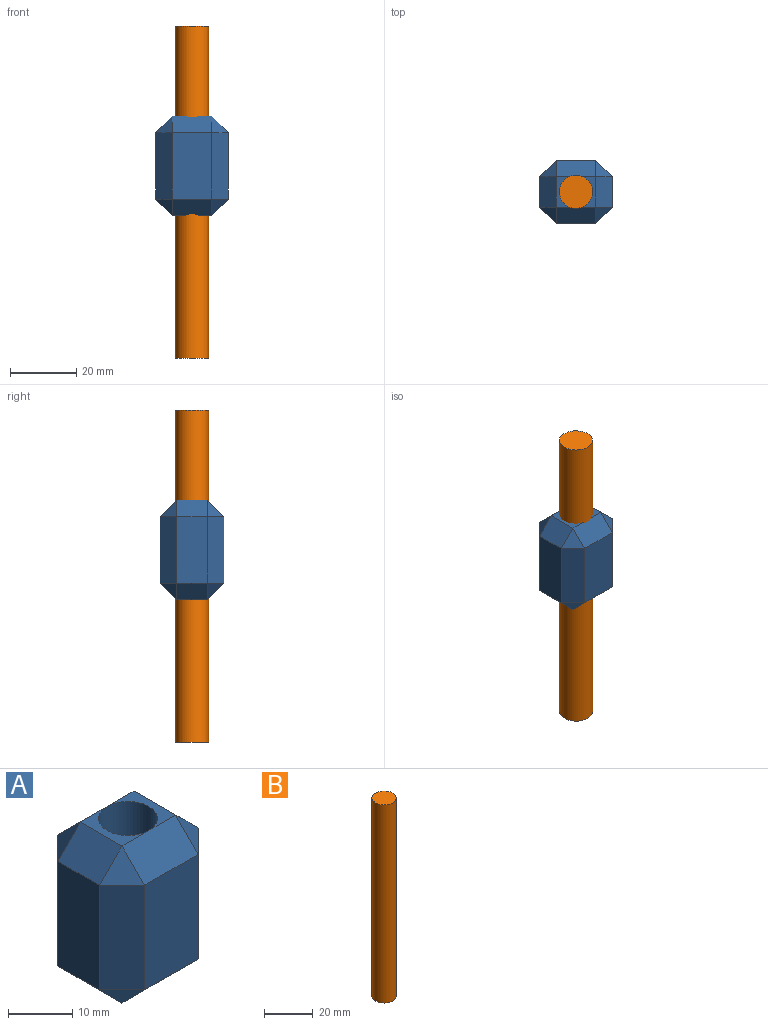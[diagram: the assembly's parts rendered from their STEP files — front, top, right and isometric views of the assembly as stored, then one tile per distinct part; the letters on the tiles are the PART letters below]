
ASSEMBLY  parts=2 mates=1
PART A: 29 faces, bbox 21.8x19.2x30 mm
  f0: plane 9.17x5.92mm, normal (0,0,1), area 21.2mm2, adj f8,f12,f13,f28
  f1: plane 9.17x5.92mm, normal (0,0,-1), area 21.2mm2, adj f16,f21,f27,f28
  f2: plane 20x11.83mm, normal (0,1,0), area 236.7mm2, adj f8,f11,f15,f16
  f3: plane 20x9.17mm, normal (-1,0,0), area 183.4mm2, adj f11,f12,f21,f22
  f4: plane 20x11.83mm, normal (0,-1,0), area 236.7mm2, adj f13,f22,f23,f27
  f5: plane 20x9.17mm, normal (1,0,0), area 183.4mm2, adj f14,f15,f23,f24
  f6: plane 9.17x5.92mm, normal (0,0,1), area 21.2mm2, adj f8,f13,f14,f28
  f7: plane 9.17x5.92mm, normal (0,0,-1), area 21.2mm2, adj f16,f24,f27,f28
  f8: plane 11.83x5mm, normal (0,0.71,0.71), area 83.7mm2, adj f0,f2,f6,f9,f10
  f9: plane 5x5mm, normal (-0.58,0.58,0.58), area 21.7mm2, adj f8,f11,f12
  f10: plane 5x5mm, normal (0.58,0.58,0.58), area 21.7mm2, adj f8,f14,f15
  f11: plane 20x5mm, normal (-0.71,0.71,0), area 141.4mm2, adj f2,f3,f9,f17
  f12: plane 9.17x5mm, normal (-0.71,0,0.71), area 64.8mm2, adj f0,f3,f9,f18
  f13: plane 11.83x5mm, normal (0,-0.71,0.71), area 83.7mm2, adj f0,f4,f6,f18,f19
  f14: plane 9.17x5mm, normal (0.71,0,0.71), area 64.8mm2, adj f5,f6,f10,f19
  f15: plane 20x5mm, normal (0.71,0.71,0), area 141.4mm2, adj f2,f5,f10,f20
  f16: plane 11.83x5mm, normal (0,0.71,-0.71), area 83.7mm2, adj f1,f2,f7,f17,f20
  f17: plane 5x5mm, normal (-0.58,0.58,-0.58), area 21.7mm2, adj f11,f16,f21
  f18: plane 5x5mm, normal (-0.58,-0.58,0.58), area 21.7mm2, adj f12,f13,f22
  f19: plane 5x5mm, normal (0.58,-0.58,0.58), area 21.7mm2, adj f13,f14,f23
  f20: plane 5x5mm, normal (0.58,0.58,-0.58), area 21.7mm2, adj f15,f16,f24
  f21: plane 9.17x5mm, normal (-0.71,0,-0.71), area 64.8mm2, adj f1,f3,f17,f25
  f22: plane 20x5mm, normal (-0.71,-0.71,0), area 141.4mm2, adj f3,f4,f18,f25
  f23: plane 20x5mm, normal (0.71,-0.71,0), area 141.4mm2, adj f4,f5,f19,f26
  f24: plane 9.17x5mm, normal (0.71,0,-0.71), area 64.8mm2, adj f5,f7,f20,f26
  f25: plane 5x5mm, normal (-0.58,-0.58,-0.58), area 21.7mm2, adj f21,f22,f27
  f26: plane 5x5mm, normal (0.58,-0.58,-0.58), area 21.7mm2, adj f23,f24,f27
  f27: plane 11.83x5mm, normal (0,-0.71,-0.71), area 83.7mm2, adj f1,f4,f7,f25,f26
  f28: cylinder r=4.59mm len=30mm, axis (0,0,1), area 864.3mm2, adj f0,f1,f6,f7
PART B: 3 faces, bbox 10x10x100 mm
  f0: cylinder r=5mm len=100mm, axis (0,0,-1), area 3141.6mm2, adj f1,f2
  f1: plane 10x10mm, normal (0,0,1), area 78.5mm2, adj f0
  f2: plane 10x10mm, normal (0,0,-1), area 78.5mm2, adj f0
PLACE A t=(63.66,-45.06,-75.47)mm
PLACE B t=(84.86,-60.68,-118.35)mm
MATE slider B.f0 <-> A.f28  axis (0,0,1) through (26.25,-13.64,-18.35)mm
